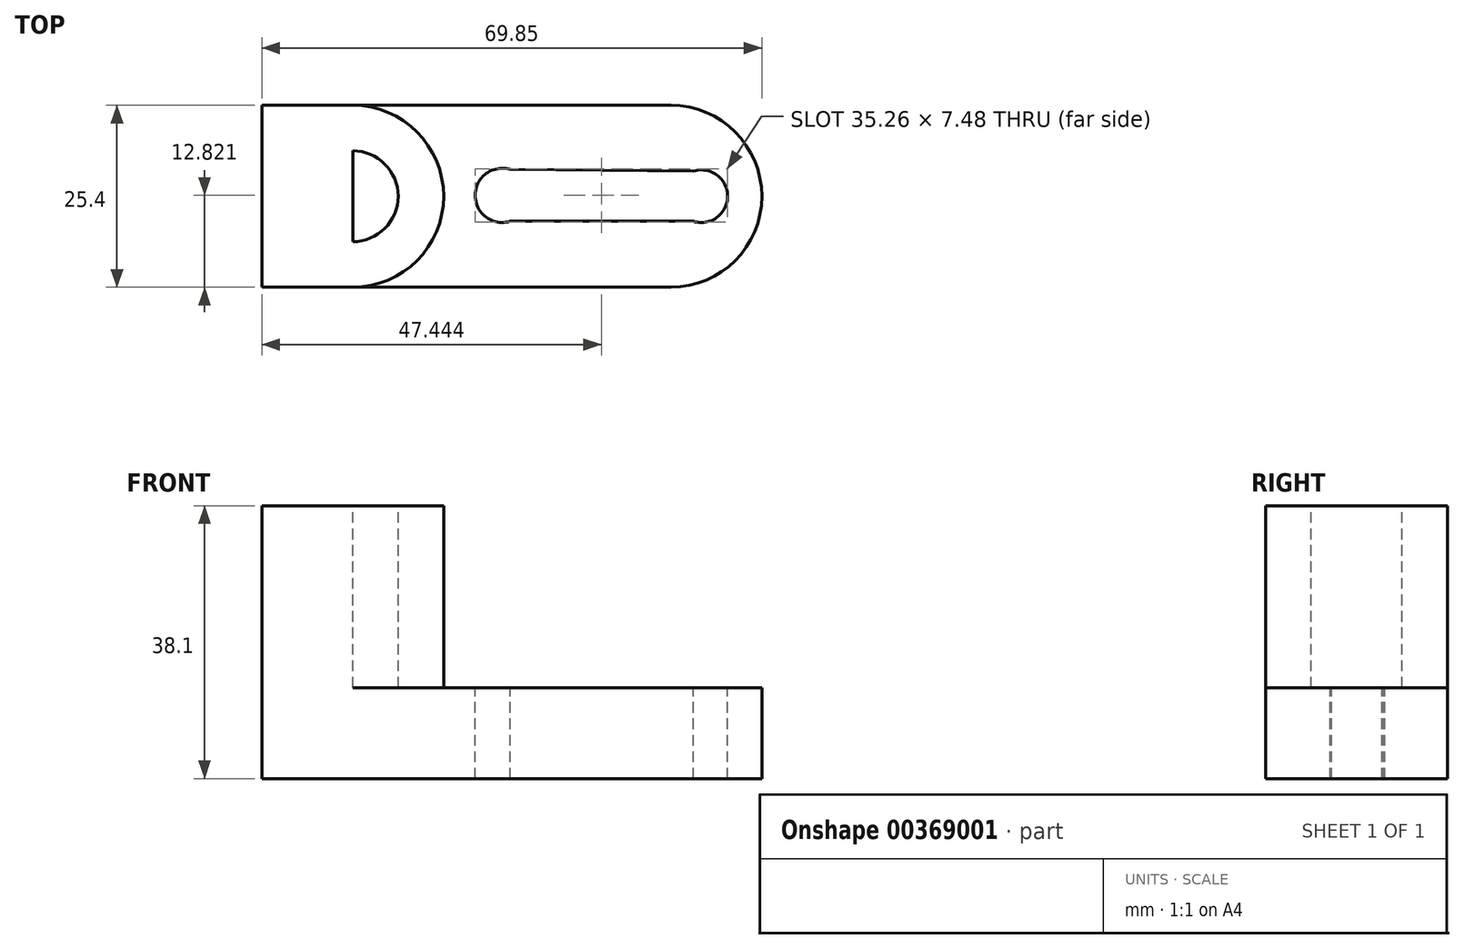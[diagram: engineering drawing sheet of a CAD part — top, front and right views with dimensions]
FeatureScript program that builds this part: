
annotation { "Feature Type Name" : "Feature", "Feature Type Description" : "" }
export const myFeature = defineFeature(function(context is Context, id is Id, definition is map)
    precondition{}
    {
        {
            var Q0;
            Q0=qCreatedBy(makeId("Front.planeOp"),FACE);
            var sketch = newSketch(context, id + "F0", { "sketchPlane" : qUnion([Q0])});
            skLineSegment(sketch, "E0", {"start": v(-30.94, 38.1) * mm, "end": v(-30.94, 0) * mm});
            skLineSegment(sketch, "E1", {"start": v(-30.94, 0) * mm, "end": v(38.91, 0) * mm});
            skLineSegment(sketch, "E2", {"start": v(38.91, 0) * mm, "end": v(38.91, 12.7) * mm});
            skLineSegment(sketch, "E3", {"start": v(38.91, 12.7) * mm, "end": v(-5.54, 12.7) * mm});
            skLineSegment(sketch, "E4", {"start": v(-5.54, 12.7) * mm, "end": v(-5.54, 38.1) * mm});
            skLineSegment(sketch, "E5", {"start": v(-5.54, 38.1) * mm, "end": v(-30.94, 38.1) * mm});
            skSolve(sketch);
        }
        {
            var Q0;
            Q0 = qSketchRegion(id + "F0", true);
            extrude(context, id + "F1", {"entities" : qUnion([Q0]), "depth" : 25.4 * mm});
        }
        {
            var Q0;
            Q0=makeQuery(id+"F1.opExtrude","SWEPT_FACE",FACE,{"disambiguationData":[OSD([sQuery(id+"F0.wireOp",EDGE,"E5")])]});
            var sketch = newSketch(context, id + "F2", { "sketchPlane" : qUnion([Q0])});
            skLineSegment(sketch, "E6", {"start": v(-30.94, 0) * mm, "end": v(-18.24, 0) * mm});
            skLineSegment(sketch, "E7", {"start": v(-5.54, -12.7) * mm, "end": v(-5.54, -12.7) * mm});
            skLineSegment(sketch, "E8", {"start": v(-18.24, -25.4) * mm, "end": v(-30.94, -25.4) * mm});
            skLineSegment(sketch, "E9", {"start": v(-30.94, -25.4) * mm, "end": v(-30.94, 0) * mm});
            skLineSegment(sketch, "E10", {"start": v(-18.24, 0) * mm, "end": v(-18.24, -25.4) * mm});
            skLineSegment(sketch, "E11", {"start": v(-30.94, -12.7) * mm, "end": v(-5.54, -12.7) * mm});
            skCircle(sketch, "E12", {"center": v(-18.24, -12.7) * mm, "radius": 6.35 * mm});
            skLineSegment(sketch, "E13", {"start": v(-18.24, -12.7) * mm, "end": v(-11.89, -12.7) * mm});
            skPoint(sketch, "E14.visualSharp", {"position": v(-5.54, 0) * mm});
            skArc(sketch, "E14.filletArc", {"start": v(-5.54, -12.7) * mm, "mid": v(-9.26, -3.72) * mm, "end": v(-18.24, 0) * mm});
            skPoint(sketch, "E15.visualSharp", {"position": v(-5.54, -25.4) * mm});
            skArc(sketch, "E15.filletArc", {"start": v(-18.24, -25.4) * mm, "mid": v(-9.26, -21.68) * mm, "end": v(-5.54, -12.7) * mm});
            skSolve(sketch);
        }
        {
            var Q0;
            {var subQ0=sQuery(id+"F2.wireOp",EDGE,"E8");var subQ1=sQuery(id+"F2.wireOp",EDGE,"E7");var subQ2=makeQuery(id+"F2.imprint","INTERSECT",VERTEX,{"derivedFrom":[subQ1,subQ0]});Q0=makeQuery(id+"F2.imprint","IMPRINT",FACE,{"disambiguationData":[TD([[makeQuery(id+"F2.imprint","IMPRINT",EDGE,{"disambiguationData":[TD([[subQ2,-1.0]])],"derivedFrom":subQ1}),1.0]])]});}
            var Q1;
            {var subQ0=sQuery(id+"F2.wireOp",EDGE,"E13");Q1=makeQuery(id+"F2.imprint","IMPRINT",FACE,{"disambiguationData":[TD([[makeQuery(id+"F2.imprint","IMPRINT",EDGE,{"derivedFrom":subQ0}),1.0]])]});}
            var Q2;
            {var subQ0=sQuery(id+"F2.wireOp",EDGE,"E13");Q2=makeQuery(id+"F2.imprint","IMPRINT",FACE,{"disambiguationData":[TD([[makeQuery(id+"F2.imprint","IMPRINT",EDGE,{"derivedFrom":subQ0}),-1.0]])]});}
            var Q3;
            {var subQ1=sQuery(id+"F2.wireOp",EDGE,"E10");var subQ3=sQuery(id+"F2.wireOp",EDGE,"E12");var subQ4=makeQuery(id+"F2.imprint","INTERSECT",VERTEX,{"disambiguationData":[OD(1.0)],"derivedFrom":[subQ1,subQ3]});Q3=makeQuery(id+"F2.imprint","IMPRINT",FACE,{"disambiguationData":[TD([[makeQuery(id+"F2.imprint","IMPRINT",EDGE,{"disambiguationData":[TD([[subQ4,1.0]])],"derivedFrom":subQ3}),1.0]])]});}
            var Q4;
            {var subQ1=sQuery(id+"F2.wireOp",EDGE,"E10");var subQ3=sQuery(id+"F2.wireOp",EDGE,"E12");var subQ4=makeQuery(id+"F2.imprint","INTERSECT",VERTEX,{"disambiguationData":[OD(0.0)],"derivedFrom":[subQ1,subQ3]});Q4=makeQuery(id+"F2.imprint","IMPRINT",FACE,{"disambiguationData":[TD([[makeQuery(id+"F2.imprint","IMPRINT",EDGE,{"disambiguationData":[TD([[subQ4,-1.0]])],"derivedFrom":subQ3}),1.0]])]});}
            var Q5;
            {var subQ0=sQuery(id+"F2.wireOp",EDGE,"E14.filletArc");Q5=makeQuery(id+"F2.imprint","IMPRINT",FACE,{"disambiguationData":[TD([[makeQuery(id+"F2.imprint","IMPRINT",EDGE,{"derivedFrom":subQ0}),-1.0]])]});}
            var Q6;
            {var subQ0=sQuery(id+"F2.wireOp",EDGE,"E15.filletArc");Q6=makeQuery(id+"F2.imprint","IMPRINT",FACE,{"disambiguationData":[TD([[makeQuery(id+"F2.imprint","IMPRINT",EDGE,{"derivedFrom":subQ0}),-1.0]])]});}
            extrude(context, id + "F3", {"entities" : qUnion([Q0, Q1, Q2, Q3, Q4, Q5, Q6]), "operationType" : NewBodyOperationType.REMOVE, "oppositeDirection" : true, "depth" : 25.4 * mm});
        }
        {
            var Q0;
            {var subQ0=sQuery(id+"F0.wireOp",EDGE,"E5");var subQ1=sQuery(id+"F0.wireOp",EDGE,"E4");Q0=makeQuery(id+"F3.boolean.opBoolean","MERGE",FACE,{"derivedFrom":[makeQuery(id+"F1.opExtrude","SWEPT_FACE",FACE,{"disambiguationData":[OSD([sQuery(id+"F0.wireOp",EDGE,"E3")])]}),makeQuery(id+"F3.opExtrude","CAP_FACE",FACE,{"disambiguationData":[OSD([subQ1,subQ0,sQuery(id+"F2.wireOp",EDGE,"E14.filletArc")])],"isStart":false}),makeQuery(id+"F3.opExtrude","CAP_FACE",FACE,{"disambiguationData":[OSD([subQ1,subQ0,sQuery(id+"F2.wireOp",EDGE,"E15.filletArc")])],"isStart":false})]});}
            var sketch = newSketch(context, id + "F4", { "sketchPlane" : qUnion([Q0])});
            skLineSegment(sketch, "E16", {"start": v(10.34, 0) * mm, "end": v(10.34, -6.35) * mm});
            skPoint(sketch, "E16.endSnap0", {"position": v(10.34, 0) * mm});
            skLineSegment(sketch, "E17", {"start": v(10.34, -6.35) * mm, "end": v(10.34, -19.05) * mm});
            skLineSegment(sketch, "E18", {"start": v(10.34, -19.05) * mm, "end": v(10.34, -25.4) * mm});
            skLineSegment(sketch, "E19", {"start": v(2.66, -8.94) * mm, "end": v(2.66, -16.2) * mm});
            skLineSegment(sketch, "E20", {"start": v(2.66, -16.2) * mm, "end": v(30.46, -16.2) * mm});
            skLineSegment(sketch, "E21", {"start": v(30.46, -16.2) * mm, "end": v(30.46, -9.19) * mm});
            skLineSegment(sketch, "E22", {"start": v(30.46, -9.19) * mm, "end": v(2.66, -8.94) * mm});
            skCircle(sketch, "E23", {"center": v(2.66, -12.57) * mm, "radius": 3.78 * mm});
            skCircle(sketch, "E24", {"center": v(30.46, -12.7) * mm, "radius": 3.68 * mm});
            skSolve(sketch);
        }
        {
            var Q0;
            Q0 = qSketchRegion(id + "F4", true);
            extrude(context, id + "F5", {"entities" : qUnion([Q0]), "operationType" : NewBodyOperationType.REMOVE, "oppositeDirection" : true, "depth" : 25.4 * mm});
        }
        {
            var Q0;
            {var subQ0=sQuery(id+"F0.wireOp",EDGE,"E5");var subQ1=sQuery(id+"F0.wireOp",EDGE,"E4");Q0=makeQuery(id+"F3.boolean.opBoolean","MERGE",FACE,{"derivedFrom":[makeQuery(id+"F1.opExtrude","SWEPT_FACE",FACE,{"disambiguationData":[OSD([sQuery(id+"F0.wireOp",EDGE,"E3")])]}),makeQuery(id+"F3.opExtrude","CAP_FACE",FACE,{"disambiguationData":[OSD([subQ1,subQ0,sQuery(id+"F2.wireOp",EDGE,"E14.filletArc")])],"isStart":false}),makeQuery(id+"F3.opExtrude","CAP_FACE",FACE,{"disambiguationData":[OSD([subQ1,subQ0,sQuery(id+"F2.wireOp",EDGE,"E15.filletArc")])],"isStart":false})]});}
            var sketch = newSketch(context, id + "F6", { "sketchPlane" : qUnion([Q0])});
            skLineSegment(sketch, "E25", {"start": v(38.91, 0) * mm, "end": v(38.91, -25.4) * mm});
            skLineSegment(sketch, "E26", {"start": v(38.91, -12.7) * mm, "end": v(38.91, -25.4) * mm});
            skLineSegment(sketch, "E27", {"start": v(-31.42, -25.4) * mm, "end": v(-30.47, 0) * mm});
            skLineSegment(sketch, "E28", {"start": v(-30.47, 0) * mm, "end": v(26.21, 0) * mm});
            skPoint(sketch, "E29.visualSharp", {"position": v(38.91, 0) * mm});
            skArc(sketch, "E29.filletArc", {"start": v(38.91, -12.7) * mm, "mid": v(35.2, -3.72) * mm, "end": v(26.21, 0) * mm});
            skSolve(sketch);
        }
        {
            var Q0;
            {var subQ0=sQuery(id+"F6.wireOp",EDGE,"E25");Q0=makeQuery(id+"F6.imprint","IMPRINT",FACE,{"disambiguationData":[TD([[makeQuery(id+"F6.imprint","IMPRINT",EDGE,{"derivedFrom":subQ0}),1.0]])]});}
            extrude(context, id + "F7", {"entities" : qUnion([Q0]), "operationType" : NewBodyOperationType.REMOVE, "oppositeDirection" : true, "depth" : 25.4 * mm});
        }
        {
            var Q0;
            {var subQ0=sQuery(id+"F0.wireOp",EDGE,"E5");var subQ1=sQuery(id+"F0.wireOp",EDGE,"E4");Q0=makeQuery(id+"F3.boolean.opBoolean","MERGE",FACE,{"derivedFrom":[makeQuery(id+"F1.opExtrude","SWEPT_FACE",FACE,{"disambiguationData":[OSD([sQuery(id+"F0.wireOp",EDGE,"E3")])]}),makeQuery(id+"F3.opExtrude","CAP_FACE",FACE,{"disambiguationData":[OSD([subQ1,subQ0,sQuery(id+"F2.wireOp",EDGE,"E14.filletArc")])],"isStart":false}),makeQuery(id+"F3.opExtrude","CAP_FACE",FACE,{"disambiguationData":[OSD([subQ1,subQ0,sQuery(id+"F2.wireOp",EDGE,"E15.filletArc")])],"isStart":false})]});}
            var sketch = newSketch(context, id + "F8", { "sketchPlane" : qUnion([Q0])});
            skLineSegment(sketch, "E30", {"start": v(38.91, -12.7) * mm, "end": v(38.91, 0) * mm});
            skLineSegment(sketch, "E31", {"start": v(38.91, 0) * mm, "end": v(0, 0) * mm});
            skLineSegment(sketch, "E32", {"start": v(0, 0) * mm, "end": v(0, -25.4) * mm});
            skLineSegment(sketch, "E33", {"start": v(0, -25.4) * mm, "end": v(26.21, -25.4) * mm});
            skPoint(sketch, "E34.visualSharp", {"position": v(38.91, -25.4) * mm});
            skArc(sketch, "E34.filletArc", {"start": v(26.21, -25.4) * mm, "mid": v(35.2, -21.68) * mm, "end": v(38.91, -12.7) * mm});
            skSolve(sketch);
        }
        {
            var Q0;
            {var subQ0=sQuery(id+"F8.wireOp",EDGE,"E34.filletArc");Q0=makeQuery(id+"F8.imprint","IMPRINT",FACE,{"disambiguationData":[TD([[makeQuery(id+"F8.imprint","IMPRINT",EDGE,{"derivedFrom":subQ0}),-1.0]])]});}
            extrude(context, id + "F9", {"entities" : qUnion([Q0]), "operationType" : NewBodyOperationType.REMOVE, "oppositeDirection" : true, "depth" : 25.4 * mm});
        }
    });
